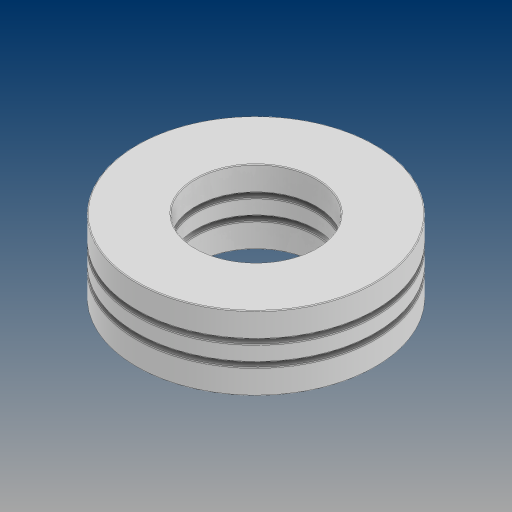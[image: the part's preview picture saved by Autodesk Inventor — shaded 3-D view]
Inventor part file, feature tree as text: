
AUTODESK INVENTOR PART (.ipt)
format: ipt  version: 2024.3 (Build 283343000, 343)  size: 333,824 bytes
history: native  units: in
note: dims shown in document units (in); Inventor stores cm internally (conversion verified against a paired STEP export)
features: fillet x3, other x2, revolve x1
ambient origin geometry x8: Origin, YZ Plane, XZ Plane, XY Plane, X Axis, Y Axis, Z Axis, Center Point
bodies: Solid1 (feature_tree), Solid2 (feature_tree), Solid3 (feature_tree), Solid4 (feature_tree), Solid5 (feature_tree), Solid6 (feature_tree)
feature tree (6):
  revolve  "Revolve2"  [1 undecoded]
  other  "CirPattern1[1]"
  other  "CirPattern1[2]"
  fillet  "Fillet2"  [1 undecoded]
  fillet  "Fillet1"  [1 undecoded]
  fillet  "Fillet3"  [1 undecoded]
note: 4 required parameter values undecoded (feature->parameter linkage not recoverable at this tier; creation-order binding heuristic only, values carry confidence <= 0.55)
